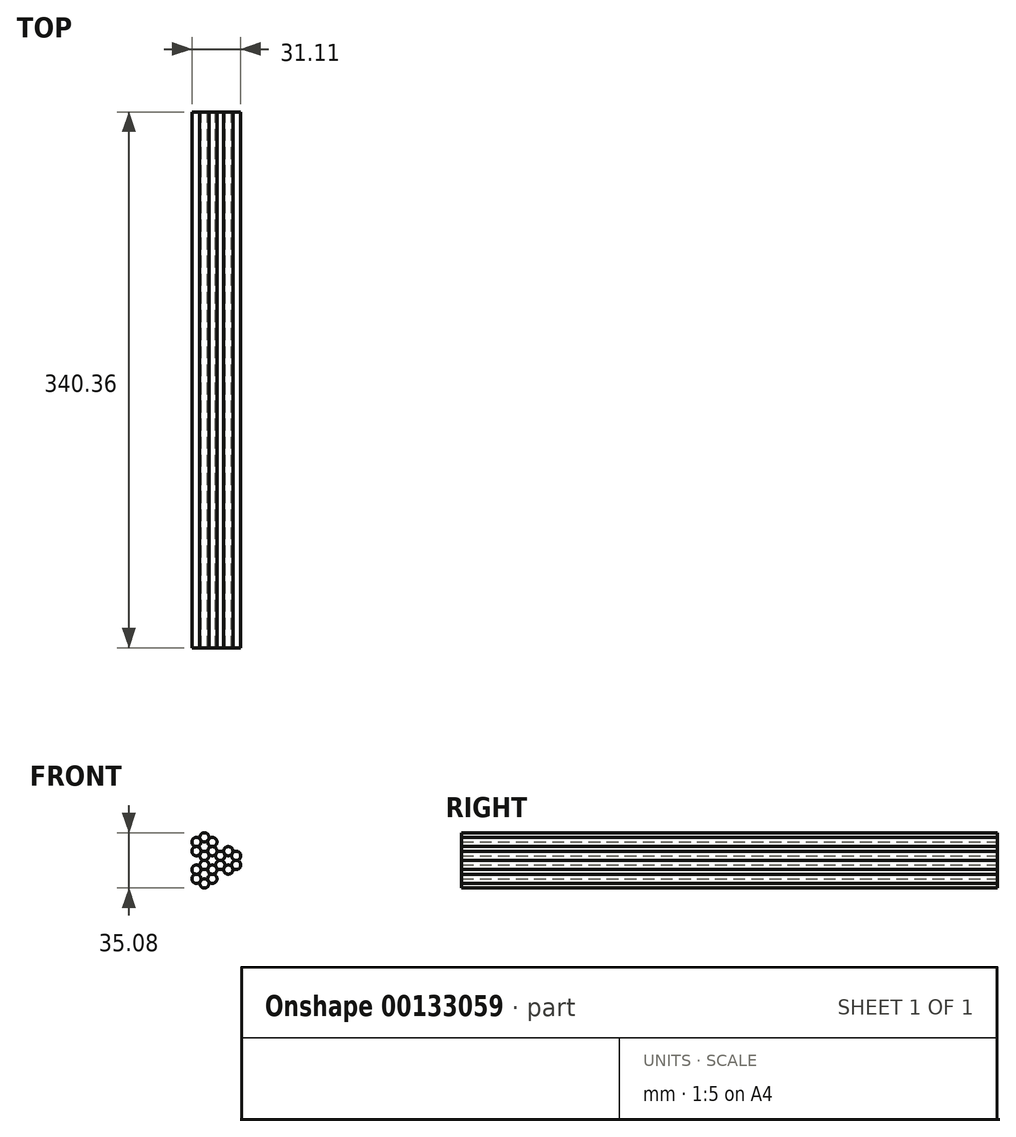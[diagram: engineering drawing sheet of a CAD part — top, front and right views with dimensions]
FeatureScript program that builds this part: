
annotation { "Feature Type Name" : "Feature", "Feature Type Description" : "" }
export const myFeature = defineFeature(function(context is Context, id is Id, definition is map)
    precondition{}
    {
        {
            var Q0;
            Q0=qCreatedBy(makeId("Front.planeOp"),FACE);
            var sketch = newSketch(context, id + "F0", { "sketchPlane" : qUnion([Q0])});
            skCircle(sketch, "E0", {"center": v(0, 0) * mm, "radius": 2.92 * mm});
            skCircle(sketch, "E1", {"center": v(5.05, -8.77) * mm, "radius": 2.92 * mm});
            skCircle(sketch, "E2", {"center": v(5.05, 2.93) * mm, "radius": 2.92 * mm});
            skCircle(sketch, "E3", {"center": v(10.1, 0) * mm, "radius": 2.92 * mm});
            skCircle(sketch, "E4", {"center": v(10.1, -5.84) * mm, "radius": 2.92 * mm});
            skCircle(sketch, "E5", {"center": v(0, -5.84) * mm, "radius": 2.92 * mm});
            skCircle(sketch, "E6", {"center": v(0, 17.54) * mm, "radius": 2.92 * mm});
            skCircle(sketch, "E7", {"center": v(5.05, 20.47) * mm, "radius": 2.92 * mm});
            skCircle(sketch, "E8", {"center": v(10.1, 17.54) * mm, "radius": 2.92 * mm});
            skCircle(sketch, "E9", {"center": v(0, 11.7) * mm, "radius": 2.92 * mm});
            skCircle(sketch, "E10", {"center": v(5.05, 8.77) * mm, "radius": 2.92 * mm});
            skCircle(sketch, "E11", {"center": v(10.1, 11.7) * mm, "radius": 2.92 * mm});
            skCircle(sketch, "E12", {"center": v(15.16, 8.77) * mm, "radius": 2.92 * mm});
            skCircle(sketch, "E13", {"center": v(15.16, 2.93) * mm, "radius": 2.92 * mm});
            skCircle(sketch, "E14", {"center": v(20.22, 11.7) * mm, "radius": 2.92 * mm});
            skCircle(sketch, "E15", {"center": v(20.22, 0) * mm, "radius": 2.92 * mm});
            skCircle(sketch, "E16", {"center": v(25.27, 2.93) * mm, "radius": 2.92 * mm});
            skCircle(sketch, "E17", {"center": v(25.27, 8.77) * mm, "radius": 2.92 * mm});
            skSolve(sketch);
        }
        {
            var Q0;
            {var subQ0=sQuery(id+"F0.wireOp",EDGE,"E10");var subQ1=makeQuery(id+"F0.imprint","INTERSECT",VERTEX,{"derivedFrom":[sQuery(id+"F0.wireOp",EDGE,"E9"),subQ0]});Q0=makeQuery(id+"F0.imprint","IMPRINT",FACE,{"disambiguationData":[TD([[makeQuery(id+"F0.imprint","IMPRINT",EDGE,{"disambiguationData":[TD([[subQ1,1.0]])],"derivedFrom":subQ0}),1.0]])]});}
            var Q1;
            {var subQ0=sQuery(id+"F0.wireOp",EDGE,"E1");var subQ1=makeQuery(id+"F0.imprint","INTERSECT",VERTEX,{"derivedFrom":[subQ0,sQuery(id+"F0.wireOp",EDGE,"E4")]});Q1=makeQuery(id+"F0.imprint","IMPRINT",FACE,{"disambiguationData":[TD([[makeQuery(id+"F0.imprint","IMPRINT",EDGE,{"disambiguationData":[TD([[subQ1,-1.0]])],"derivedFrom":subQ0}),1.0]])]});}
            var Q2;
            {var subQ0=sQuery(id+"F0.wireOp",EDGE,"E0");var subQ1=makeQuery(id+"F0.imprint","INTERSECT",VERTEX,{"derivedFrom":[subQ0,sQuery(id+"F0.wireOp",EDGE,"E2")]});Q2=makeQuery(id+"F0.imprint","IMPRINT",FACE,{"disambiguationData":[TD([[makeQuery(id+"F0.imprint","IMPRINT",EDGE,{"disambiguationData":[TD([[subQ1,-1.0]])],"derivedFrom":subQ0}),1.0]])]});}
            var Q3;
            {var subQ0=sQuery(id+"F0.wireOp",EDGE,"E12");var subQ1=makeQuery(id+"F0.imprint","INTERSECT",VERTEX,{"derivedFrom":[sQuery(id+"F0.wireOp",EDGE,"E11"),subQ0]});Q3=makeQuery(id+"F0.imprint","IMPRINT",FACE,{"disambiguationData":[TD([[makeQuery(id+"F0.imprint","IMPRINT",EDGE,{"disambiguationData":[TD([[subQ1,1.0]])],"derivedFrom":subQ0}),1.0]])]});}
            var Q4;
            {var subQ0=sQuery(id+"F0.wireOp",EDGE,"E3");var subQ1=makeQuery(id+"F0.imprint","INTERSECT",VERTEX,{"derivedFrom":[subQ0,sQuery(id+"F0.wireOp",EDGE,"E13")]});Q4=makeQuery(id+"F0.imprint","IMPRINT",FACE,{"disambiguationData":[TD([[makeQuery(id+"F0.imprint","IMPRINT",EDGE,{"disambiguationData":[TD([[subQ1,-1.0]])],"derivedFrom":subQ0}),1.0]])]});}
            var Q5;
            {var subQ0=sQuery(id+"F0.wireOp",EDGE,"E11");var subQ1=makeQuery(id+"F0.imprint","INTERSECT",VERTEX,{"derivedFrom":[sQuery(id+"F0.wireOp",EDGE,"E8"),subQ0]});Q5=makeQuery(id+"F0.imprint","IMPRINT",FACE,{"disambiguationData":[TD([[makeQuery(id+"F0.imprint","IMPRINT",EDGE,{"disambiguationData":[TD([[subQ1,-1.0]])],"derivedFrom":subQ0}),1.0]])]});}
            var Q6;
            {var subQ0=sQuery(id+"F0.wireOp",EDGE,"E4");var subQ1=makeQuery(id+"F0.imprint","INTERSECT",VERTEX,{"derivedFrom":[sQuery(id+"F0.wireOp",EDGE,"E1"),subQ0]});Q6=makeQuery(id+"F0.imprint","IMPRINT",FACE,{"disambiguationData":[TD([[makeQuery(id+"F0.imprint","IMPRINT",EDGE,{"disambiguationData":[TD([[subQ1,1.0]])],"derivedFrom":subQ0}),1.0]])]});}
            var Q7;
            {var subQ0=sQuery(id+"F0.wireOp",EDGE,"E5");var subQ1=makeQuery(id+"F0.imprint","INTERSECT",VERTEX,{"derivedFrom":[sQuery(id+"F0.wireOp",EDGE,"E0"),subQ0]});Q7=makeQuery(id+"F0.imprint","IMPRINT",FACE,{"disambiguationData":[TD([[makeQuery(id+"F0.imprint","IMPRINT",EDGE,{"disambiguationData":[TD([[subQ1,1.0]])],"derivedFrom":subQ0}),1.0]])]});}
            var Q8;
            {var subQ0=sQuery(id+"F0.wireOp",EDGE,"E6");var subQ1=makeQuery(id+"F0.imprint","INTERSECT",VERTEX,{"derivedFrom":[subQ0,sQuery(id+"F0.wireOp",EDGE,"E7")]});Q8=makeQuery(id+"F0.imprint","IMPRINT",FACE,{"disambiguationData":[TD([[makeQuery(id+"F0.imprint","IMPRINT",EDGE,{"disambiguationData":[TD([[subQ1,-1.0]])],"derivedFrom":subQ0}),1.0]])]});}
            var Q9;
            {var subQ0=sQuery(id+"F0.wireOp",EDGE,"E13");var subQ1=makeQuery(id+"F0.imprint","INTERSECT",VERTEX,{"derivedFrom":[sQuery(id+"F0.wireOp",EDGE,"E3"),subQ0]});Q9=makeQuery(id+"F0.imprint","IMPRINT",FACE,{"disambiguationData":[TD([[makeQuery(id+"F0.imprint","IMPRINT",EDGE,{"disambiguationData":[TD([[subQ1,1.0]])],"derivedFrom":subQ0}),1.0]])]});}
            var Q10;
            {var subQ0=sQuery(id+"F0.wireOp",EDGE,"E7");var subQ1=makeQuery(id+"F0.imprint","INTERSECT",VERTEX,{"derivedFrom":[sQuery(id+"F0.wireOp",EDGE,"E6"),subQ0]});Q10=makeQuery(id+"F0.imprint","IMPRINT",FACE,{"disambiguationData":[TD([[makeQuery(id+"F0.imprint","IMPRINT",EDGE,{"disambiguationData":[TD([[subQ1,-1.0]])],"derivedFrom":subQ0}),1.0]])]});}
            var Q11;
            {var subQ0=sQuery(id+"F0.wireOp",EDGE,"E17");var subQ1=makeQuery(id+"F0.imprint","INTERSECT",VERTEX,{"derivedFrom":[sQuery(id+"F0.wireOp",EDGE,"E14"),subQ0]});Q11=makeQuery(id+"F0.imprint","IMPRINT",FACE,{"disambiguationData":[TD([[makeQuery(id+"F0.imprint","IMPRINT",EDGE,{"disambiguationData":[TD([[subQ1,-1.0]])],"derivedFrom":subQ0}),1.0]])]});}
            var Q12;
            {var subQ0=sQuery(id+"F0.wireOp",EDGE,"E8");var subQ1=makeQuery(id+"F0.imprint","INTERSECT",VERTEX,{"derivedFrom":[sQuery(id+"F0.wireOp",EDGE,"E7"),subQ0]});Q12=makeQuery(id+"F0.imprint","IMPRINT",FACE,{"disambiguationData":[TD([[makeQuery(id+"F0.imprint","IMPRINT",EDGE,{"disambiguationData":[TD([[subQ1,-1.0]])],"derivedFrom":subQ0}),1.0]])]});}
            var Q13;
            {var subQ0=sQuery(id+"F0.wireOp",EDGE,"E14");var subQ1=makeQuery(id+"F0.imprint","INTERSECT",VERTEX,{"derivedFrom":[sQuery(id+"F0.wireOp",EDGE,"E12"),subQ0]});Q13=makeQuery(id+"F0.imprint","IMPRINT",FACE,{"disambiguationData":[TD([[makeQuery(id+"F0.imprint","IMPRINT",EDGE,{"disambiguationData":[TD([[subQ1,-1.0]])],"derivedFrom":subQ0}),1.0]])]});}
            var Q14;
            {var subQ0=sQuery(id+"F0.wireOp",EDGE,"E9");var subQ1=makeQuery(id+"F0.imprint","INTERSECT",VERTEX,{"derivedFrom":[sQuery(id+"F0.wireOp",EDGE,"E6"),subQ0]});Q14=makeQuery(id+"F0.imprint","IMPRINT",FACE,{"disambiguationData":[TD([[makeQuery(id+"F0.imprint","IMPRINT",EDGE,{"disambiguationData":[TD([[subQ1,-1.0]])],"derivedFrom":subQ0}),1.0]])]});}
            var Q15;
            {var subQ0=sQuery(id+"F0.wireOp",EDGE,"E15");var subQ1=makeQuery(id+"F0.imprint","INTERSECT",VERTEX,{"derivedFrom":[sQuery(id+"F0.wireOp",EDGE,"E13"),subQ0]});Q15=makeQuery(id+"F0.imprint","IMPRINT",FACE,{"disambiguationData":[TD([[makeQuery(id+"F0.imprint","IMPRINT",EDGE,{"disambiguationData":[TD([[subQ1,1.0]])],"derivedFrom":subQ0}),1.0]])]});}
            var Q16;
            {var subQ0=sQuery(id+"F0.wireOp",EDGE,"E16");var subQ1=makeQuery(id+"F0.imprint","INTERSECT",VERTEX,{"derivedFrom":[sQuery(id+"F0.wireOp",EDGE,"E15"),subQ0]});Q16=makeQuery(id+"F0.imprint","IMPRINT",FACE,{"disambiguationData":[TD([[makeQuery(id+"F0.imprint","IMPRINT",EDGE,{"disambiguationData":[TD([[subQ1,1.0]])],"derivedFrom":subQ0}),1.0]])]});}
            var Q17;
            {var subQ0=sQuery(id+"F0.wireOp",EDGE,"E2");var subQ1=makeQuery(id+"F0.imprint","INTERSECT",VERTEX,{"derivedFrom":[sQuery(id+"F0.wireOp",EDGE,"E0"),subQ0]});Q17=makeQuery(id+"F0.imprint","IMPRINT",FACE,{"disambiguationData":[TD([[makeQuery(id+"F0.imprint","IMPRINT",EDGE,{"disambiguationData":[TD([[subQ1,1.0]])],"derivedFrom":subQ0}),1.0]])]});}
            extrude(context, id + "F1", {"entities" : qUnion([Q0, Q1, Q2, Q3, Q4, Q5, Q6, Q7, Q8, Q9, Q10, Q11, Q12, Q13, Q14, Q15, Q16, Q17]), "depth" : 340.36 * mm});
        }
    });
